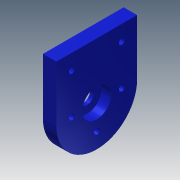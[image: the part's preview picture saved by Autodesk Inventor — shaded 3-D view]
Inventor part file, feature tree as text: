
AUTODESK INVENTOR PART (.ipt)
format: ipt  version: 2013 (Build 170138000, 138)  size: 124,928 bytes
history: native  units: mm
features: sketch x7, extrude x5
ambient origin geometry x8: Origin, YZ Plane, XZ Plane, XY Plane, X Axis, Y Axis, Z Axis, Center Point
bodies: Solid1 (feature_tree)
feature tree (12):
  extrude  "Extrusion1"  Depth=6.0mm TaperAngle=0.0deg
  extrude  "Extrusion2"  Depth=7.0mm
  extrude  "Extrusion3"  Depth=8.0mm TaperAngle=0.0deg
  extrude  "Extrusion4"  [1 undecoded]
  extrude  "Extrusion5"  [1 undecoded]
  sketch  "Sketch6"
  sketch  "Sketch7"
  sketch  "Sketch1"  dims[d4=5.0mm d5=0.0mm d7=6.0mm d8=0.0mm]
  sketch  "Sketch2"  dims[d9=2.0mm d10=0.0mm d11=7.0mm]
  sketch  "Sketch3"  dims[d12=2.0mm d13=0.0mm d25=8.0mm d26=0.0mm]
  sketch  "Sketch4"
  sketch  "Sketch5"
note: 2 required parameter values undecoded (feature->parameter linkage not recoverable at this tier; creation-order binding heuristic only, values carry confidence <= 0.55)
